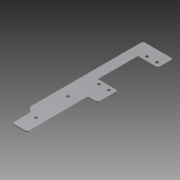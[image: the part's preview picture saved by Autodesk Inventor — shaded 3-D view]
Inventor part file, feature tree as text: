
AUTODESK INVENTOR PART (.ipt)
format: ipt  version: 2012 (Build 160160000, 160)  size: 168,448 bytes
history: native  units: mm
features: sketch x2, extrude x1, plane x1, hole x1
ambient origin geometry x8: Origin, YZ Plane, XZ Plane, XY Plane, X Axis, Y Axis, Z Axis, Center Point
feature tree (5):
  extrude  "Extrusion2"  Depth=10.0mm
  plane  "Work Plane1"
  hole  "Hole1"  [1 undecoded]
  sketch  "Sketch1"  dims[d0=5.0mm d1=20.0mm d2=3.0mm d3=5.0mm d4=4.0mm d5=3.0mm d6=10.0mm d7=3.0mm d8=3.0mm d9=10.0mm d10=5.0mm d11=4.0mm d14=15.0mm d15=135.75mm d18=10.0mm]
  sketch  "Sketch4"  dims[d19=15.0mm d21=30.0mm d22=2.0mm d23=5.0mm d26=3.0mm d27=3.0mm d29=30.0mm d30=1.0mm d31=0.0mm d32=0.0mm d33=5.0mm d34=20.0mm d35=3.0mm d36=5.0mm d37=4.0mm d38=3.0mm d39=10.0mm d40=3.0mm d41=3.0mm d42=10.0mm d43=5.0mm d44=4.0mm d45=15.0mm d46=135.75mm d47=10.0mm d48=15.0mm d49=30.0mm d50=2.0mm d51=5.0mm d52=3.0mm d53=3.0mm d54=30.0mm d55=3.0mm d56=6.0mm d57=4.0mm d58=2.0mm d59=90.0deg d60=8.0mm d61=20.594885mm d62=48.0mm d63=48.0mm]
note: 1 required parameter value undecoded (feature->parameter linkage not recoverable at this tier; creation-order binding heuristic only, values carry confidence <= 0.55)
